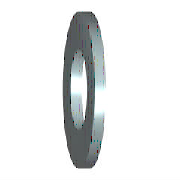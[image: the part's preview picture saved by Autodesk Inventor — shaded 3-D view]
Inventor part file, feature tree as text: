
AUTODESK INVENTOR PART (.ipt)
format: ipt  version: 2015 (Build 190159000, 159)  size: 112,128 bytes
history: native  units: mm (DEFAULTED — no unit token found)
features: other x1, plane x1, sketch x1
ambient origin geometry x7: Origin, YZ Plane, XY Plane, X Axis, Y Axis, Z Axis, Center Point
bodies: Solid1 (feature_tree), Body (feature_tree)
feature tree (3):
  other  "Work Axis1"
  plane  "Work Plane1"
  sketch  "Sketch"  dims[d0=8.4mm d1=16.0mm d2=1.6mm d3=0.0mm d4=0.0mm d5=0.0mm d6=0.0mm d7=0.0mm]
